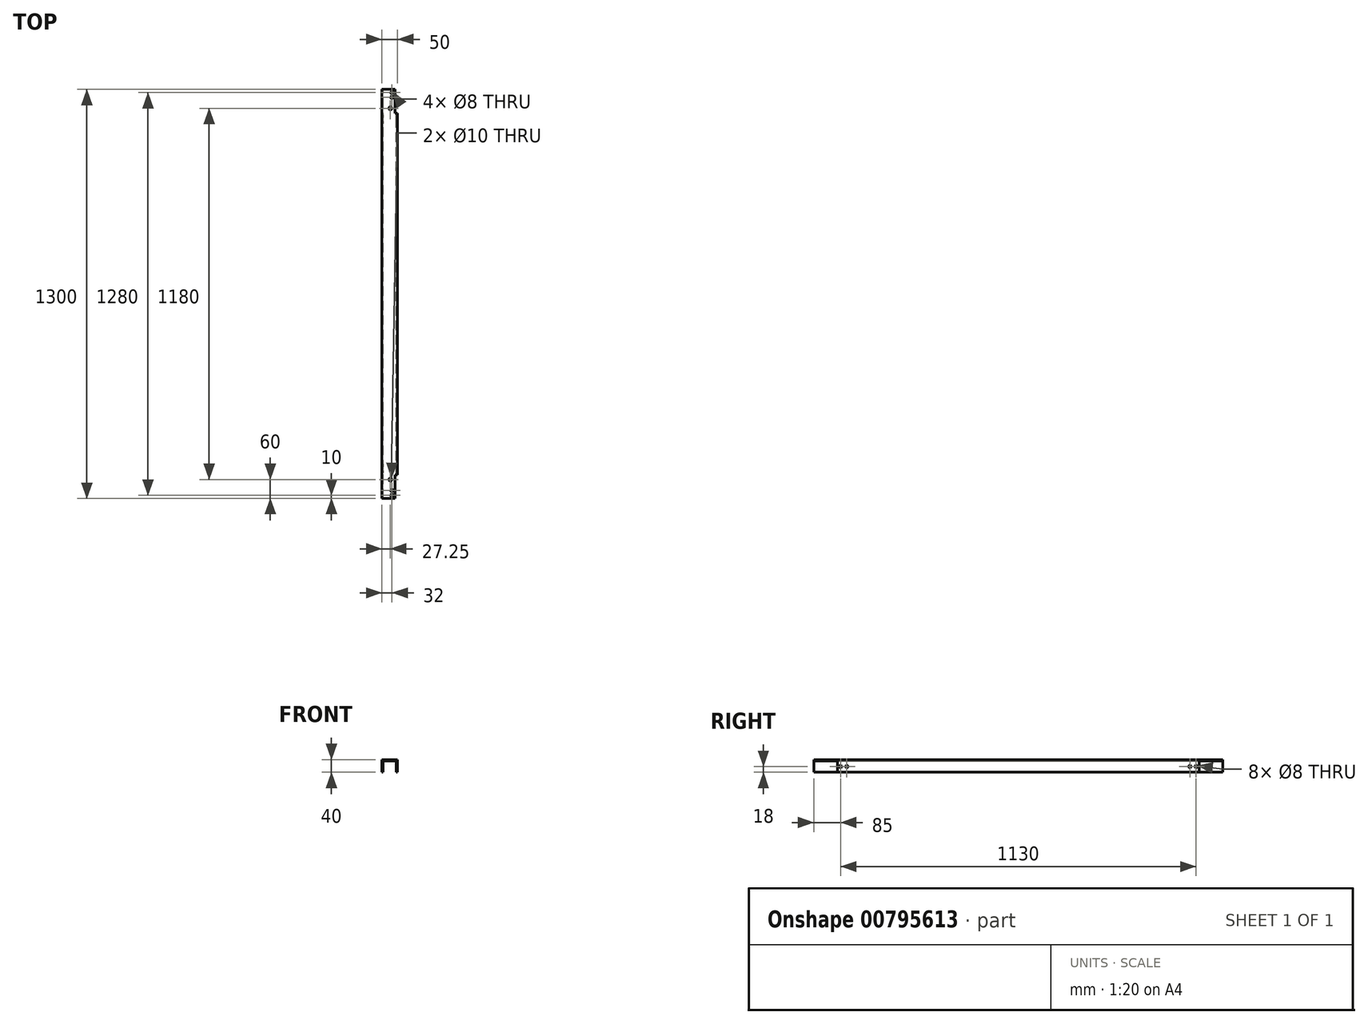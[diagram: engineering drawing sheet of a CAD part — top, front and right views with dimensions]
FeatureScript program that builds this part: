
annotation { "Feature Type Name" : "Feature", "Feature Type Description" : "" }
export const myFeature = defineFeature(function(context is Context, id is Id, definition is map)
    precondition{}
    {
        {
            var Q0;
            Q0=qCreatedBy(makeId("Front.planeOp"),FACE);
            var sketch = newSketch(context, id + "F0", { "sketchPlane" : qUnion([Q0])});
            skLineSegment(sketch, "E0.bottom", {"start": v(25, -20) * mm, "end": v(21, -20) * mm});
            skLineSegment(sketch, "E0.top", {"start": v(25, 20) * mm, "end": v(-25, 20) * mm});
            skLineSegment(sketch, "E0.left", {"start": v(25, -20) * mm, "end": v(25, 20) * mm});
            skLineSegment(sketch, "E0.right", {"start": v(-25, -20) * mm, "end": v(-25, 20) * mm});
            skPoint(sketch, "E0.middle", {"position": v(0, 0) * mm});
            skLineSegment(sketch, "E1", {"start": v(-21, -20) * mm, "end": v(-21, 16) * mm});
            skLineSegment(sketch, "E2", {"start": v(-21, 16) * mm, "end": v(21, 16) * mm});
            skLineSegment(sketch, "E3", {"start": v(21, 16) * mm, "end": v(21, -20) * mm});
            skLineSegment(sketch, "E4.trimOffspring", {"start": v(-21, -20) * mm, "end": v(-25, -20) * mm});
            skSolve(sketch);
        }
        {
            var Q0;
            Q0=makeQuery(id+"F0.imprint","IMPRINT",FACE,{"disambiguationData":[TD([[makeQuery(id+"F0.imprint","IMPRINT",EDGE,{"derivedFrom":sQuery(id+"F0.wireOp",EDGE,"E0.bottom")}),-1.0]])]});
            extrude(context, id + "F1", {"entities" : qUnion([Q0]), "endBound" : BoundingType.SYMMETRIC, "depth" : 1300 * mm, "offsetDistance" : 25.4 * mm});
        }
        {
            var Q0;
            Q0=makeQuery(id+"F1.opExtrude","SWEPT_FACE",FACE,{"disambiguationData":[OSD([sQuery(id+"F0.wireOp",EDGE,"E0.left")])]});
            var sketch = newSketch(context, id + "F2", { "sketchPlane" : qUnion([Q0])});
            skLineSegment(sketch, "E5", {"start": v(-650, 20) * mm, "end": v(-575, 20) * mm});
            skLineSegment(sketch, "E6", {"start": v(-575, 20) * mm, "end": v(-575, -20) * mm});
            skLineSegment(sketch, "E7", {"start": v(-575, -20) * mm, "end": v(-650, -20) * mm});
            skLineSegment(sketch, "E8", {"start": v(-650, -20) * mm, "end": v(-650, 20) * mm});
            skLineSegment(sketch, "E9.MirrorCS", {"start": v(575, 20) * mm, "end": v(575, -20) * mm});
            skLineSegment(sketch, "E10.MirrorCS", {"start": v(650, 20) * mm, "end": v(575, 20) * mm});
            skLineSegment(sketch, "E11.MirrorCS", {"start": v(650, -20) * mm, "end": v(650, 20) * mm});
            skLineSegment(sketch, "E12.MirrorCS", {"start": v(575, -20) * mm, "end": v(650, -20) * mm});
            skCircle(sketch, "E13", {"center": v(-565, -2) * mm, "radius": 4 * mm});
            skCircle(sketch, "E14", {"center": v(-545, -2) * mm, "radius": 4 * mm});
            skCircle(sketch, "E15.MirrorC", {"center": v(565, -2) * mm, "radius": 4 * mm});
            skCircle(sketch, "E16.MirrorC", {"center": v(545, -2) * mm, "radius": 4 * mm});
            skSolve(sketch);
        }
        {
            var Q0;
            Q0=makeQuery(id+"F2.imprint","IMPRINT",FACE,{"disambiguationData":[TD([[makeQuery(id+"F2.imprint","IMPRINT",EDGE,{"derivedFrom":sQuery(id+"F2.wireOp",EDGE,"E5")}),-1.0]])]});
            var Q1;
            Q1=makeQuery(id+"F2.imprint","IMPRINT",FACE,{"disambiguationData":[TD([[makeQuery(id+"F2.imprint","IMPRINT",EDGE,{"derivedFrom":sQuery(id+"F2.wireOp",EDGE,"E9.MirrorCS")}),1.0]])]});
            extrude(context, id + "F3", {"entities" : qUnion([Q0, Q1]), "operationType" : NewBodyOperationType.REMOVE, "oppositeDirection" : true, "depth" : 8 * mm, "offsetDistance" : 25 * mm});
        }
        {
            var Q0;
            Q0=makeQuery(id+"F1.opExtrude","SWEPT_FACE",FACE,{"disambiguationData":[OSD([sQuery(id+"F0.wireOp",EDGE,"E0.top")])]});
            var sketch = newSketch(context, id + "F4", { "sketchPlane" : qUnion([Q0])});
            skCircle(sketch, "E17", {"center": v(7, -640) * mm, "radius": 4 * mm});
            skCircle(sketch, "E18", {"center": v(7, -625) * mm, "radius": 4 * mm});
            skCircle(sketch, "E19.MirrorC", {"center": v(7, 625) * mm, "radius": 4 * mm});
            skCircle(sketch, "E20.MirrorC", {"center": v(7, 640) * mm, "radius": 4 * mm});
            skCircle(sketch, "E21", {"center": v(2.25, -590) * mm, "radius": 5 * mm});
            skCircle(sketch, "E22.MirrorC", {"center": v(2.25, 590) * mm, "radius": 5 * mm});
            skSolve(sketch);
        }
        {
            var Q0;
            Q0=sQuery(id+"F4.wireOp",VERTEX,"E18.center");
            var Q1;
            Q1=sQuery(id+"F4.wireOp",VERTEX,"E17.center");
            var Q2;
            Q2=sQuery(id+"F4.wireOp",VERTEX,"E20.MirrorC.center");
            var Q3;
            Q3=sQuery(id+"F4.wireOp",VERTEX,"E19.MirrorC.center");
            var Q4;
            Q4=sQuery(id+"F2.wireOp",VERTEX,"E13.center");
            var Q5;
            Q5=sQuery(id+"F2.wireOp",VERTEX,"E14.center");
            var Q6;
            Q6=sQuery(id+"F2.wireOp",VERTEX,"E15.MirrorC.center");
            var Q7;
            Q7=sQuery(id+"F2.wireOp",VERTEX,"E16.MirrorC.center");
            var Q8;
            Q8=makeQuery(id+"F1.opExtrude","SWEPT_BODY",BODY,{"disambiguationData":[OSD([sQuery(id+"F0.wireOp",EDGE,"E0.bottom"),sQuery(id+"F0.wireOp",EDGE,"E0.top"),sQuery(id+"F0.wireOp",EDGE,"E0.left"),sQuery(id+"F0.wireOp",EDGE,"E0.right"),sQuery(id+"F0.wireOp",EDGE,"E1"),sQuery(id+"F0.wireOp",EDGE,"E2"),sQuery(id+"F0.wireOp",EDGE,"E3"),sQuery(id+"F0.wireOp",EDGE,"E4.trimOffspring")])]});
            hole(context, id + "F5", {"style" : HoleStyle.SIMPLE, "endStyle" : HoleEndStyle.THROUGH, "standardTappedOrClearance" : lookupTablePath({ "standard" : "ISO", "size" : "8", "type" : "Drilled" }), "standardBlindInLast" : lookupTablePath({ "standard" : "ISO", "size" : "8", "type" : "Drilled" }), "holeDiameter" : 8 * mm, "majorDiameter" : 5 * mm, "isTappedThrough" : true, "tappedDepth" : 12.7 * mm, "tapClearance" : 3, "locations" : qUnion([Q0, Q1, Q2, Q3, Q4, Q5, Q6, Q7]), "scope" : qUnion([Q8])});
        }
        {
            var Q0;
            Q0=sQuery(id+"F4.wireOp",VERTEX,"E21.center");
            var Q1;
            Q1=sQuery(id+"F4.wireOp",VERTEX,"E22.MirrorC.center");
            var Q2;
            Q2=makeQuery(id+"F1.opExtrude","SWEPT_BODY",BODY,{"disambiguationData":[OSD([sQuery(id+"F0.wireOp",EDGE,"E0.bottom"),sQuery(id+"F0.wireOp",EDGE,"E0.top"),sQuery(id+"F0.wireOp",EDGE,"E0.left"),sQuery(id+"F0.wireOp",EDGE,"E0.right"),sQuery(id+"F0.wireOp",EDGE,"E1"),sQuery(id+"F0.wireOp",EDGE,"E2"),sQuery(id+"F0.wireOp",EDGE,"E3"),sQuery(id+"F0.wireOp",EDGE,"E4.trimOffspring")])]});
            hole(context, id + "F6", {"style" : HoleStyle.SIMPLE, "endStyle" : HoleEndStyle.THROUGH, "standardTappedOrClearance" : lookupTablePath({ "standard" : "ISO", "size" : "10", "type" : "Drilled" }), "standardBlindInLast" : lookupTablePath({ "standard" : "ISO", "size" : "10", "type" : "Drilled" }), "holeDiameter" : 10 * mm, "majorDiameter" : 5 * mm, "isTappedThrough" : true, "tappedDepth" : 12.7 * mm, "tapClearance" : 3, "locations" : qUnion([Q0, Q1]), "scope" : qUnion([Q2])});
        }
    });
